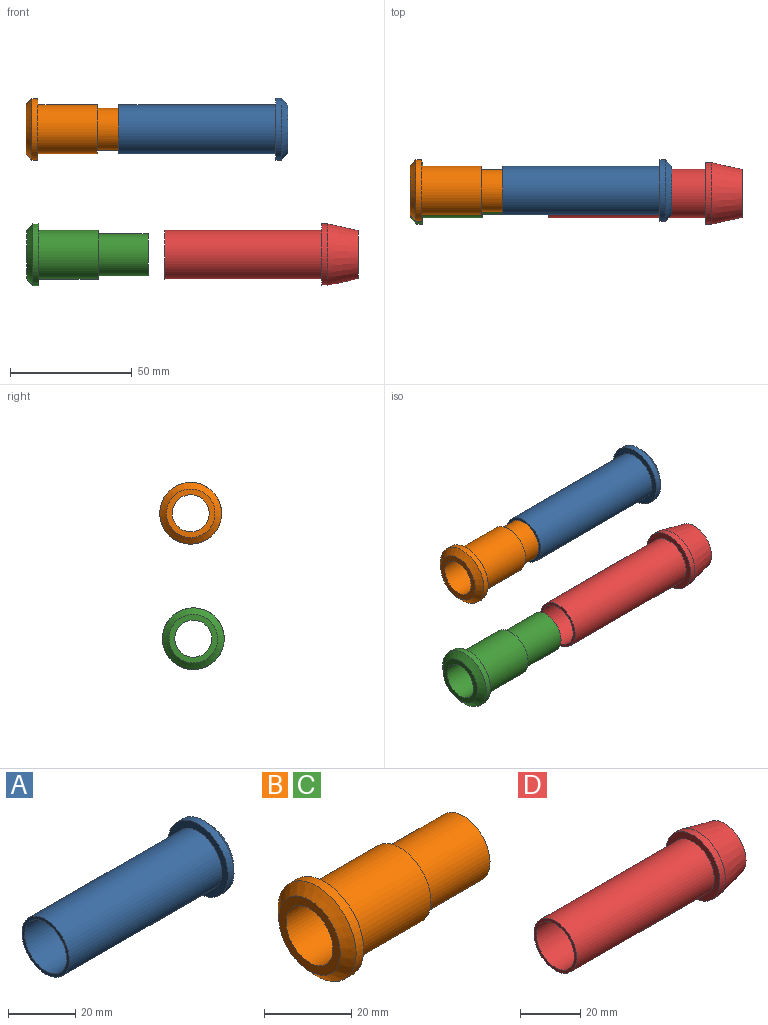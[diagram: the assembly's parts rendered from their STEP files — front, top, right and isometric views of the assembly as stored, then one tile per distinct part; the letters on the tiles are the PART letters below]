
ASSEMBLY  parts=4 mates=2
PART A: 9 faces, bbox 69.3x25.3x25.3 mm
  f0: cylinder r=10mm len=64.4mm, axis (-1,0,0), area 4046.4mm2, adj f1,f8
  f1: plane 20x20mm, normal (-1,0,0), area 68.1mm2, adj f0,f2
  f2: cylinder r=8.85mm len=19.5mm, axis (-1,0,0), area 1084.3mm2, adj f1,f3
  f3: plane 17.7x17.7mm, normal (-1,0,0), area 64.6mm2, adj f2,f4
  f4: cylinder r=7.6mm len=49.8mm, axis (-1,0,0), area 2378.1mm2, adj f3,f5
  f5: plane 19.92x19.92mm, normal (1,0,0), area 130.3mm2, adj f4,f6
  f6: cone r=9.96mm half-angle=47.7deg, axis (-1,0,0), area 258.1mm2, adj f5,f7
  f7: cylinder r=12.65mm len=25.3mm, axis (-1,0,0), area 195.2mm2, adj f6,f8
  f8: plane 25.3x25.3mm, normal (-1,0,0), area 188.6mm2, adj f0,f7
PART B: 9 faces, bbox 49.8x25.3x25.3 mm
  f0: cylinder r=10mm len=24.4mm, axis (1,0,0), area 1533.1mm2, adj f1,f8
  f1: plane 25.3x25.3mm, normal (1,0,0), area 188.6mm2, adj f0,f2
  f2: cylinder r=12.65mm len=25.3mm, axis (1,0,0), area 195.2mm2, adj f1,f3
  f3: cone r=9.96mm half-angle=47.7deg, axis (1,0,0), area 258.1mm2, adj f2,f4
  f4: plane 19.92x19.92mm, normal (-1,0,0), area 130.3mm2, adj f3,f5
  f5: cylinder r=7.6mm len=49.8mm, axis (1,0,0), area 2378.1mm2, adj f4,f6
  f6: plane 17.3x17.3mm, normal (1,0,0), area 53.6mm2, adj f5,f7
  f7: cylinder r=8.65mm len=20.5mm, axis (1,0,0), area 1114.2mm2, adj f6,f8
  f8: plane 20x20mm, normal (1,0,0), area 79.1mm2, adj f0,f7
PART C: same geometry as B
PART D: 9 faces, bbox 79.3x25.3x25.3 mm
  f0: cylinder r=10mm len=64.4mm, axis (-1,0,0), area 4046.4mm2, adj f1,f8
  f1: plane 20x20mm, normal (-1,0,0), area 68.1mm2, adj f0,f2
  f2: cylinder r=8.85mm len=19.5mm, axis (-1,0,0), area 1084.3mm2, adj f1,f3
  f3: plane 17.7x17.7mm, normal (-1,0,0), area 64.6mm2, adj f2,f4
  f4: cylinder r=7.6mm len=59.8mm, axis (-1,0,0), area 2855.6mm2, adj f3,f5
  f5: plane 19.84x19.84mm, normal (1,0,0), area 127.7mm2, adj f4,f6
  f6: cone r=9.92mm half-angle=12.4deg, axis (-1,0,0), area 901mm2, adj f5,f7
  f7: cylinder r=12.65mm len=25.3mm, axis (-1,0,0), area 197.8mm2, adj f6,f8
  f8: plane 25.3x25.3mm, normal (-1,0,0), area 188.6mm2, adj f0,f7
PLACE A t=(10.88,8.82,9.92)mm
PLACE B t=(3.27,8.82,9.92)mm
PLACE C t=(3.57,7.75,-41.54)mm
PLACE D t=(29.69,7.75,-41.54)mm
MATE slider C.f0 <-> D.f0  axis (1,0,0) through (3.47,7.75,-41.54)mm
MATE cylindrical A.f0 <-> B.f0  axis (-1,0,0) through (-8.52,8.82,9.92)mm
